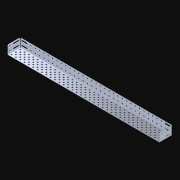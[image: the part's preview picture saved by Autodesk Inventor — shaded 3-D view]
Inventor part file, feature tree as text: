
AUTODESK INVENTOR PART (.ipt)
format: ipt  version: 2021 (Build 250183000, 183)  size: 3,463,680 bytes
history: native  units: in
note: dims shown in document units (in); Inventor stores cm internally (conversion verified against a paired STEP export)
features: other x240, extrude x239, pattern_linear x5, imported_body x1, sketch x1
ambient origin geometry x8: Origin, YZ Plane, XZ Plane, XY Plane, X Axis, Y Axis, Z Axis, Center Point
bodies: Body1 (feature_tree), Body2 (feature_tree), Body3 (feature_tree), Body4 (feature_tree), Body5 (feature_tree), Body6 (feature_tree), Body7 (feature_tree), Body8 (feature_tree), Body9 (feature_tree), Body10 (feature_tree), Body11 (feature_tree), Body12 (feature_tree), Body13 (feature_tree), Body14 (feature_tree), Body15 (feature_tree), Body16 (feature_tree), Body17 (feature_tree), Body18 (feature_tree), Body19 (feature_tree), Body20 (feature_tree), Body21 (feature_tree), Body22 (feature_tree), Body23 (feature_tree), Body24 (feature_tree), Body25 (feature_tree), Body26 (feature_tree), Body27 (feature_tree), Body28 (feature_tree), Body29 (feature_tree), Body30 (feature_tree), Body31 (feature_tree), Body32 (feature_tree), Body33 (feature_tree), Body34 (feature_tree), Body35 (feature_tree), Body36 (feature_tree), Body37 (feature_tree), Body38 (feature_tree), Body39 (feature_tree), Body40 (feature_tree), Body41 (feature_tree), Body42 (feature_tree), Body43 (feature_tree), Body44 (feature_tree), Body45 (feature_tree), Body46 (feature_tree), Body47 (feature_tree), Body48 (feature_tree), Body49 (feature_tree), Body50 (feature_tree), Body51 (feature_tree), Body52 (feature_tree), Body53 (feature_tree), Body54 (feature_tree), Body55 (feature_tree), Body56 (feature_tree), Body57 (feature_tree), Body58 (feature_tree), Body59 (feature_tree), Body60 (feature_tree), Body61 (feature_tree), Body62 (feature_tree), Body63 (feature_tree), Body64 (feature_tree), Body65 (feature_tree), Body66 (feature_tree), Body67 (feature_tree), Body68 (feature_tree), Body69 (feature_tree), Body70 (feature_tree), Body71 (feature_tree), Body72 (feature_tree), Body73 (feature_tree), Body74 (feature_tree), Body75 (feature_tree), Body76 (feature_tree), Body77 (feature_tree), Body78 (feature_tree), Body79 (feature_tree), Body80 (feature_tree), Body81 (feature_tree), Body82 (feature_tree), Body83 (feature_tree), Body84 (feature_tree), Body85 (feature_tree), Body86 (feature_tree), Body87 (feature_tree), Body88 (feature_tree), Body89 (feature_tree), Body90 (feature_tree), Body91 (feature_tree), Body92 (feature_tree), Body93 (feature_tree), Body94 (feature_tree), Body95 (feature_tree), Body96 (feature_tree), Body97 (feature_tree), Body98 (feature_tree), Body99 (feature_tree), Body100 (feature_tree), Body101 (feature_tree), Body102 (feature_tree), Body103 (feature_tree), Body104 (feature_tree), Body105 (feature_tree), Body106 (feature_tree), Body107 (feature_tree), Body108 (feature_tree), Body109 (feature_tree), Body110 (feature_tree), Body111 (feature_tree), Body112 (feature_tree), Body113 (feature_tree), Body114 (feature_tree), Body115 (feature_tree), Body116 (feature_tree), Body117 (feature_tree), Body118 (feature_tree), Body119 (feature_tree), Body120 (feature_tree), Body121 (feature_tree), Body122 (feature_tree), Body123 (feature_tree), Body124 (feature_tree), Body125 (feature_tree), Body126 (feature_tree), Body127 (feature_tree), Body128 (feature_tree), Body129 (feature_tree), Body130 (feature_tree), Body131 (feature_tree), Body132 (feature_tree), Body133 (feature_tree), Body134 (feature_tree), Body135 (feature_tree), Body136 (feature_tree), Body137 (feature_tree), Body138 (feature_tree), Body139 (feature_tree), Body140 (feature_tree), Body141 (feature_tree), Body142 (feature_tree), Body143 (feature_tree), Body144 (feature_tree), Body145 (feature_tree), Body146 (feature_tree), Body147 (feature_tree), Body148 (feature_tree), Body149 (feature_tree), Body150 (feature_tree), Body151 (feature_tree), Body152 (feature_tree), Body153 (feature_tree), Body154 (feature_tree), Body155 (feature_tree), Body156 (feature_tree), Body157 (feature_tree), Body158 (feature_tree), Body159 (feature_tree), Body160 (feature_tree), Body161 (feature_tree), Body162 (feature_tree), Body163 (feature_tree), Body164 (feature_tree), Body165 (feature_tree), Body166 (feature_tree), Body167 (feature_tree), Body168 (feature_tree), Body169 (feature_tree), Body170 (feature_tree), Body171 (feature_tree), Body172 (feature_tree), Body173 (feature_tree), Body174 (feature_tree), Body175 (feature_tree), Body176 (feature_tree), Body177 (feature_tree), Body178 (feature_tree), Body179 (feature_tree), Body180 (feature_tree), Body181 (feature_tree), Body182 (feature_tree), Body183 (feature_tree), Body184 (feature_tree), Body185 (feature_tree), Body186 (feature_tree), Body187 (feature_tree), Body188 (feature_tree), Body189 (feature_tree), Body190 (feature_tree), Body191 (feature_tree), Body192 (feature_tree), Body193 (feature_tree), Body194 (feature_tree), Body195 (feature_tree), Body196 (feature_tree), Body197 (feature_tree), Body198 (feature_tree), Body199 (feature_tree), Body200 (feature_tree), Body201 (feature_tree), Body202 (feature_tree), Body203 (feature_tree), Body204 (feature_tree), Body205 (feature_tree), Body206 (feature_tree), Body207 (feature_tree), Body208 (feature_tree), Body209 (feature_tree), Body210 (feature_tree), Body211 (feature_tree), Body212 (feature_tree), Body213 (feature_tree), Body214 (feature_tree), Body215 (feature_tree), Body216 (feature_tree), Body217 (feature_tree), Body218 (feature_tree), Body219 (feature_tree), Body220 (feature_tree), Body221 (feature_tree), Body222 (feature_tree), Body223 (feature_tree), Body224 (feature_tree), Body225 (feature_tree), Body226 (feature_tree), Body227 (feature_tree), Body228 (feature_tree), Body229 (feature_tree), Body230 (feature_tree), Body231 (feature_tree), Body232 (feature_tree), Body233 (feature_tree), Body234 (feature_tree), Body235 (feature_tree), Body236 (feature_tree), Body237 (feature_tree), Body238 (feature_tree), Body239 (feature_tree), Body240 (feature_tree)
feature tree (486):
  parser-record x1  (decoder bookkeeping rows leaked as tree rows — omitted from the tree; the rows remain in map.json)
  imported_body  "Base1"
  pattern_linear  "Rectangular Pattern1"  Count1=35 Spacing1=0.5in
  pattern_linear  "Rectangular Pattern2"  Count1=3 Spacing1=0.5in
  pattern_linear  "Rectangular Pattern3"  Spacing1=0.167in  [1 undecoded]
  pattern_linear  "Rectangular Pattern4"  Spacing1=0.046in  [1 undecoded]
  pattern_linear  "Rectangular Pattern5"  Count1=34 Spacing1=0.5in
  other  "Srf1"
  other  "Srf2"
  other  "Srf3"
  other  "Srf4"
  other  "Srf5"
  other  "Srf6"
  other  "Srf7"
  other  "Srf8"
  other  "Srf9"
  other  "Srf10"
  other  "Srf11"
  other  "Srf12"
  other  "Srf13"
  other  "Srf14"
  other  "Srf15"
  other  "Srf16"
  other  "Srf17"
  other  "Srf18"
  other  "Srf19"
  other  "Srf20"
  other  "Srf21"
  other  "Srf22"
  other  "Srf23"
  other  "Srf24"
  other  "Srf25"
  other  "Srf26"
  other  "Srf27"
  other  "Srf28"
  other  "Srf29"
  other  "Srf30"
  other  "Srf31"
  other  "Srf32"
  other  "Srf33"
  other  "Srf34"
  other  "Srf35"
  other  "Srf36"
  other  "Srf37"
  other  "Srf38"
  other  "Srf39"
  other  "Srf40"
  other  "Srf41"
  other  "Srf42"
  other  "Srf43"
  other  "Srf44"
  other  "Srf45"
  other  "Srf46"
  other  "Srf47"
  other  "Srf48"
  other  "Srf49"
  other  "Srf50"
  other  "Srf51"
  other  "Srf52"
  other  "Srf53"
  other  "Srf54"
  other  "Srf55"
  other  "Srf56"
  other  "Srf57"
  other  "Srf58"
  other  "Srf59"
  other  "Srf60"
  other  "Srf61"
  other  "Srf62"
  other  "Srf63"
  other  "Srf64"
  other  "Srf65"
  other  "Srf66"
  other  "Srf67"
  other  "Srf68"
  other  "Srf69"
  other  "Srf70"
  other  "Srf71"
  other  "Srf72"
  other  "Srf73"
  other  "Srf74"
  other  "Srf75"
  other  "Srf76"
  other  "Srf77"
  other  "Srf78"
  other  "Srf79"
  other  "Srf80"
  other  "Srf81"
  other  "Srf82"
  other  "Srf83"
  other  "Srf84"
  other  "Srf85"
  other  "Srf86"
  other  "Srf87"
  other  "Srf88"
  other  "Srf89"
  other  "Srf90"
  other  "Srf91"
  other  "Srf92"
  other  "Srf93"
  other  "Srf94"
  other  "Srf95"
  other  "Srf96"
  other  "Srf97"
  other  "Srf98"
  other  "Srf99"
  other  "Srf100"
  other  "Srf101"
  other  "Srf102"
  other  "Srf103"
  other  "Srf104"
  other  "Srf105"
  sketch  "Sketch10"  dims[d125=0.046in d126=0.0in d127=13.7795in d129=0.5in d130=1.1811in d132=0.5in d133=0.167in d134=0.046in d135=0.0in d136=13.3858in d138=0.5in d139=0.7874in d141=0.5in d143=0.046in d144=0.0in d145=0.7874in d147=0.5in d149=0.046in d150=0.0in d151=12.2047in d153=0.5in d154=0.7874in d156=0.5in d158=0.046in d159=0.0in d160=0.7874in d162=0.5in d163=0.0in d164=0.0in d165=0.0in d166=0.0in d167=0.0in d168=0.0in d169=0.0in d170=0.0in d171=0.0in d172=0.0in d173=0.0in d174=0.0in d175=0.0in d176=0.0in d177=0.0in d178=0.0in d179=0.0in d180=0.0in d181=0.0in d182=0.0in d183=0.0in d184=0.0in d185=0.0in d186=0.0in d187=0.0in d188=0.0in d189=0.0in d190=0.0in d191=0.0in d192=0.0in d193=0.0in d194=0.0in d195=0.0in d196=0.0in d197=0.0in d198=0.0in d199=0.0in d200=0.0in d201=0.0in d202=0.0in d203=0.0in d204=0.0in d205=0.0in d206=0.0in d207=0.0in d208=0.0in d209=0.0in d210=0.0in d211=0.0in d212=0.0in d213=0.0in d214=0.0in d215=0.0in d216=0.0in d217=0.0in d218=0.0in d219=0.0in d220=0.0in d221=0.0in d222=0.0in d223=0.0in d224=0.0in d225=0.0in d226=0.0in d227=0.0in d228=0.0in d229=0.0in d230=0.0in d231=0.0in d232=0.0in d233=0.0in d234=0.0in d235=0.0in d236=0.0in d237=0.0in d238=0.0in d239=0.0in d240=0.0in d241=0.0in d242=0.0in d243=0.0in d244=0.0in d245=0.0in d246=0.0in d247=0.0in d248=0.0in d249=0.0in d250=0.0in d251=0.0in d252=0.0in d253=0.0in d254=0.0in d255=0.0in d256=0.0in d257=0.0in d258=0.0in d259=0.0in d260=0.0in d261=0.0in d262=0.0in d263=0.0in d264=0.0in d265=0.0in d266=0.0in d267=0.0in d268=0.0in d269=0.0in d270=0.0in d271=0.0in d272=0.0in d273=0.0in d274=0.0in d275=0.0in d276=0.0in d277=0.0in d278=0.0in d279=0.0in d280=0.0in d281=0.0in d282=0.0in d283=0.0in d284=0.0in d285=0.0in d286=0.0in d287=0.0in d288=0.0in d289=0.0in d290=0.0in d291=0.0in d292=0.0in d293=0.0in d294=0.0in d295=0.0in d296=0.0in d297=0.0in d298=0.0in d299=0.0in d300=0.0in d301=0.0in d302=0.0in d303=0.0in d304=0.0in d305=0.0in d306=0.0in d307=0.0in d308=0.0in d309=0.0in d310=0.0in d311=0.0in d312=0.0in d313=0.0in d314=0.0in d315=0.0in d316=0.0in d317=0.0in d318=0.0in d319=0.0in d320=0.0in d321=0.0in d322=0.0in d323=0.0in d324=0.0in d325=0.0in d326=0.0in d327=0.0in d328=0.0in d329=0.0in d330=0.0in d331=0.0in d332=0.0in d333=0.0in d334=0.0in d335=0.0in d336=0.0in d337=0.0in d338=0.0in d339=0.0in d340=0.0in d341=0.0in d342=0.0in d343=0.0in d344=0.0in d345=0.0in d346=0.0in d347=0.0in d348=0.0in d349=0.0in d350=0.0in d351=0.0in d352=0.0in d353=0.0in d354=0.0in d355=0.0in d356=0.0in d357=0.0in d358=0.0in d359=0.0in d360=0.0in d361=0.0in d362=0.0in d363=0.0in d364=0.0in d365=0.0in d366=0.0in d367=0.0in d368=0.0in d369=0.0in d370=0.0in d371=0.0in d372=0.0in d373=0.0in d374=0.0in d375=0.0in d376=0.0in d377=0.0in d378=0.0in d379=0.0in d380=0.0in d381=0.0in d382=0.0in d383=0.0in d384=0.0in d385=0.0in d386=0.0in d387=0.0in d388=0.0in d389=0.0in d390=0.0in d391=0.0in d392=0.0in d393=0.0in d394=0.0in d395=0.0in d396=0.0in d397=0.0in d398=0.0in d399=0.0in d400=0.0in d401=0.0in d402=0.0in d403=0.0in d404=0.0in d405=0.0in d406=0.0in d407=0.0in d408=0.0in d409=0.0in d410=0.0in d411=0.0in d412=0.0in d413=0.0in d414=0.0in d415=0.0in d416=0.0in d417=0.0in d418=0.0in d419=0.0in d420=0.0in d421=0.0in d422=0.0in d423=0.0in d424=0.0in d425=0.0in d426=0.0in d427=0.0in d428=0.0in d429=0.0in d430=0.0in d431=0.0in d432=0.0in d433=0.0in d434=0.0in d435=0.0in d436=0.0in d437=0.0in d438=0.0in d439=0.0in d440=0.0in d441=0.0in d442=0.0in d443=0.0in d444=0.0in d445=0.0in d446=0.0in d447=0.0in d448=0.0in d449=0.0in d450=0.0in d451=0.0in d452=0.0in d453=0.0in d454=0.0in d455=0.0in d456=0.0in d457=0.0in d458=0.0in d459=0.0in d460=0.0in d461=0.0in d462=0.0in d463=0.0in d464=0.0in d465=0.0in d466=0.0in d467=0.0in d468=0.0in d469=0.0in d470=0.0in d471=0.0in d472=0.0in d473=0.0in d474=0.0in d475=0.0in d476=0.0in d477=0.0in d478=0.0in d479=0.0in d480=0.0in d481=0.0in d482=0.0in d483=0.0in d484=0.0in d485=0.0in d486=0.0in d487=0.0in d488=0.0in d489=0.0in d490=0.0in d491=0.0in d492=0.0in d493=0.0in d494=0.0in d495=0.0in d496=0.0in d497=0.0in d498=0.0in d499=0.0in d500=0.0in d501=0.0in d502=0.0in d503=0.0in d504=0.0in d505=0.0in d506=0.0in d507=0.0in d508=0.0in d509=0.0in d510=0.0in d511=0.0in d512=0.0in d513=0.0in d514=0.0in d515=0.0in d516=0.0in d517=0.0in d518=0.0in d519=0.0in d520=0.0in d521=0.0in d522=0.0in d523=0.0in d524=0.0in d525=0.0in d526=0.0in d527=0.0in d528=0.0in d529=0.0in d530=0.0in d531=0.0in d532=0.0in d533=0.0in d534=0.0in d535=0.0in d536=0.0in d537=0.0in d538=0.0in d539=0.0in d540=0.0in d541=0.0in d542=0.0in d543=0.0in d544=0.0in d545=0.0in d546=0.0in d547=0.0in d548=0.0in d549=0.0in d550=0.0in d551=0.0in d552=0.0in d553=0.0in d554=0.0in d555=0.0in d556=0.0in d557=0.0in d558=0.0in d559=0.0in d560=0.0in d561=0.0in d562=0.0in d563=0.0in d564=0.0in d565=0.0in d566=0.0in d567=0.0in d568=0.0in d569=0.0in d570=0.0in d571=0.0in d572=0.0in d573=0.0in d574=0.0in d575=0.0in d576=0.0in d577=0.0in d578=0.0in d579=0.0in d580=0.0in d581=0.0in d582=0.0in d583=0.0in d584=0.0in d585=0.0in d586=0.0in d587=0.0in d588=0.0in d589=0.0in d590=0.0in d591=0.0in d592=0.0in d593=0.0in d594=0.0in d595=0.0in d596=0.0in d597=0.0in d598=0.0in d599=0.0in d600=0.0in d601=0.0in d602=0.0in d603=0.0in d604=0.0in d605=0.0in d606=0.0in d607=0.0in d608=0.0in d609=0.0in d610=0.0in d611=0.0in d612=0.0in d613=0.0in d614=0.0in d615=0.0in d616=0.0in d617=0.0in d618=0.0in d619=0.0in d620=0.0in d621=0.0in d622=0.0in d623=0.0in d624=0.0in d625=0.0in d626=0.0in d627=0.0in d628=0.0in d629=0.0in d630=0.0in d631=0.0in d632=0.0in d633=0.0in d634=0.0in d635=0.0in d636=0.0in d637=0.0in d638=0.0in d639=0.0in d640=0.0in]
  other  "Srf106"
  other  "Srf107"
  other  "Srf108"
  other  "Srf109"
  other  "Srf110"
  other  "Srf111"
  other  "Srf112"
  other  "Srf113"
  other  "Srf114"
  other  "Srf115"
  other  "Srf116"
  other  "Srf117"
  other  "Srf118"
  other  "Srf119"
  other  "Srf120"
  other  "Srf121"
  other  "Srf122"
  other  "Srf123"
  other  "Srf124"
  other  "Srf125"
  other  "Srf126"
  other  "Srf127"
  other  "Srf128"
  other  "Srf129"
  other  "Srf130"
  other  "Srf131"
  other  "Srf132"
  other  "Srf133"
  other  "Srf134"
  other  "Srf135"
  other  "Srf136"
  other  "Srf137"
  other  "Srf138"
  other  "Srf139"
  other  "Srf140"
  other  "Srf141"
  other  "Srf142"
  other  "Srf143"
  other  "Srf144"
  other  "Srf145"
  other  "Srf146"
  other  "Srf147"
  other  "Srf148"
  other  "Srf149"
  other  "Srf150"
  other  "Srf151"
  other  "Srf152"
  other  "Srf153"
  other  "Srf154"
  other  "Srf155"
  other  "Srf156"
  other  "Srf157"
  other  "Srf158"
  other  "Srf159"
  other  "Srf160"
  other  "Srf161"
  other  "Srf162"
  other  "Srf163"
  other  "Srf164"
  other  "Srf165"
  other  "Srf166"
  other  "Srf167"
  other  "Srf168"
  other  "Srf169"
  other  "Srf170"
  other  "Srf171"
  other  "Srf172"
  other  "Srf173"
  other  "Srf174"
  other  "Srf175"
  other  "Srf176"
  other  "Srf177"
  other  "Srf178"
  other  "Srf179"
  other  "Srf180"
  other  "Srf181"
  other  "Srf182"
  other  "Srf183"
  other  "Srf184"
  other  "Srf185"
  other  "Srf186"
  other  "Srf187"
  other  "Srf188"
  other  "Srf189"
  other  "Srf190"
  other  "Srf191"
  other  "Srf192"
  other  "Srf193"
  other  "Srf194"
  other  "Srf195"
  other  "Srf196"
  other  "Srf197"
  other  "Srf198"
  other  "Srf199"
  other  "Srf200"
  other  "Srf201"
  other  "Srf202"
  other  "Srf203"
  other  "Srf204"
  other  "Srf205"
  other  "Srf206"
  other  "Srf207"
  other  "Srf208"
  other  "Srf209"
  other  "Srf210"
  other  "Srf211"
  other  "Srf212"
  other  "Srf213"
  other  "Srf214"
  other  "Srf215"
  other  "Srf216"
  other  "Srf217"
  other  "Srf218"
  other  "Srf219"
  other  "Srf220"
  other  "Srf221"
  other  "Srf222"
  other  "Srf223"
  other  "Srf224"
  other  "Srf225"
  other  "Srf226"
  other  "Srf227"
  other  "Srf228"
  other  "Srf229"
  other  "Srf230"
  other  "Srf231"
  other  "Srf232"
  other  "Srf233"
  other  "Srf234"
  other  "Srf235"
  other  "Srf236"
  other  "Srf237"
  other  "Srf238"
  other  "Srf239"
  extrude  "ExtrusionSrf1"  Depth=0.5in
  extrude  "ExtrusionSrf106"  Depth=0.046in TaperAngle=0.0deg
  extrude  "ExtrusionSrf174"  Depth=0.5in
  extrude  "ExtrusionSrf176"  Depth=0.046in TaperAngle=0.0deg
  extrude  "ExtrusionSrf238"  Depth=0.5in
  extrude  "ExtrusionSrf2"  Depth=0.5in
  extrude  "ExtrusionSrf3"  Depth=0.046in TaperAngle=0.0deg
  extrude  "ExtrusionSrf4"  Depth=0.5in
  extrude  "ExtrusionSrf5"  [1 undecoded]
  extrude  "ExtrusionSrf6"  [1 undecoded]
  extrude  "ExtrusionSrf7"  [1 undecoded]
  extrude  "ExtrusionSrf8"  [1 undecoded]
  extrude  "ExtrusionSrf9"  [1 undecoded]
  extrude  "ExtrusionSrf10"  [1 undecoded]
  extrude  "ExtrusionSrf11"  [1 undecoded]
  extrude  "ExtrusionSrf12"  [1 undecoded]
  extrude  "ExtrusionSrf13"  [1 undecoded]
  extrude  "ExtrusionSrf14"  [1 undecoded]
  extrude  "ExtrusionSrf15"  [1 undecoded]
  extrude  "ExtrusionSrf16"  [1 undecoded]
  extrude  "ExtrusionSrf17"  [1 undecoded]
  extrude  "ExtrusionSrf18"  [1 undecoded]
  extrude  "ExtrusionSrf19"  [1 undecoded]
  extrude  "ExtrusionSrf20"  [1 undecoded]
  extrude  "ExtrusionSrf21"  [1 undecoded]
  extrude  "ExtrusionSrf22"  [1 undecoded]
  extrude  "ExtrusionSrf23"  [1 undecoded]
  extrude  "ExtrusionSrf24"  [1 undecoded]
  extrude  "ExtrusionSrf25"  [1 undecoded]
  extrude  "ExtrusionSrf26"  [1 undecoded]
  extrude  "ExtrusionSrf27"  [1 undecoded]
  extrude  "ExtrusionSrf28"  [1 undecoded]
  extrude  "ExtrusionSrf29"  [1 undecoded]
  extrude  "ExtrusionSrf30"  [1 undecoded]
  extrude  "ExtrusionSrf31"  [1 undecoded]
  extrude  "ExtrusionSrf32"  [1 undecoded]
  extrude  "ExtrusionSrf33"  [1 undecoded]
  extrude  "ExtrusionSrf34"  [1 undecoded]
  extrude  "ExtrusionSrf35"  [1 undecoded]
  extrude  "ExtrusionSrf36"  [1 undecoded]
  extrude  "ExtrusionSrf37"  [1 undecoded]
  extrude  "ExtrusionSrf38"  [1 undecoded]
  extrude  "ExtrusionSrf39"  [1 undecoded]
  extrude  "ExtrusionSrf40"  [1 undecoded]
  extrude  "ExtrusionSrf41"  [1 undecoded]
  extrude  "ExtrusionSrf42"  [1 undecoded]
  extrude  "ExtrusionSrf43"  [1 undecoded]
  extrude  "ExtrusionSrf44"  [1 undecoded]
  extrude  "ExtrusionSrf45"  [1 undecoded]
  extrude  "ExtrusionSrf46"  [1 undecoded]
  extrude  "ExtrusionSrf47"  [1 undecoded]
  extrude  "ExtrusionSrf48"  [1 undecoded]
  extrude  "ExtrusionSrf49"  [1 undecoded]
  extrude  "ExtrusionSrf50"  [1 undecoded]
  extrude  "ExtrusionSrf51"  [1 undecoded]
  extrude  "ExtrusionSrf52"  [1 undecoded]
  extrude  "ExtrusionSrf53"  [1 undecoded]
  extrude  "ExtrusionSrf54"  [1 undecoded]
  extrude  "ExtrusionSrf55"  [1 undecoded]
  extrude  "ExtrusionSrf56"  [1 undecoded]
  extrude  "ExtrusionSrf57"  [1 undecoded]
  extrude  "ExtrusionSrf58"  [1 undecoded]
  extrude  "ExtrusionSrf59"  [1 undecoded]
  extrude  "ExtrusionSrf60"  [1 undecoded]
  extrude  "ExtrusionSrf61"  [1 undecoded]
  extrude  "ExtrusionSrf62"  [1 undecoded]
  extrude  "ExtrusionSrf63"  [1 undecoded]
  extrude  "ExtrusionSrf64"  [1 undecoded]
  extrude  "ExtrusionSrf65"  [1 undecoded]
  extrude  "ExtrusionSrf66"  [1 undecoded]
  extrude  "ExtrusionSrf67"  [1 undecoded]
  extrude  "ExtrusionSrf68"  [1 undecoded]
  extrude  "ExtrusionSrf69"  [1 undecoded]
  extrude  "ExtrusionSrf70"  [1 undecoded]
  extrude  "ExtrusionSrf71"  [1 undecoded]
  extrude  "ExtrusionSrf72"  [1 undecoded]
  extrude  "ExtrusionSrf73"  [1 undecoded]
  extrude  "ExtrusionSrf74"  [1 undecoded]
  extrude  "ExtrusionSrf75"  [1 undecoded]
  extrude  "ExtrusionSrf76"  [1 undecoded]
  extrude  "ExtrusionSrf77"  [1 undecoded]
  extrude  "ExtrusionSrf78"  [1 undecoded]
  extrude  "ExtrusionSrf79"  [1 undecoded]
  extrude  "ExtrusionSrf80"  [1 undecoded]
  extrude  "ExtrusionSrf81"  [1 undecoded]
  extrude  "ExtrusionSrf82"  [1 undecoded]
  extrude  "ExtrusionSrf83"  [1 undecoded]
  extrude  "ExtrusionSrf84"  [1 undecoded]
  extrude  "ExtrusionSrf85"  [1 undecoded]
  extrude  "ExtrusionSrf86"  [1 undecoded]
  extrude  "ExtrusionSrf87"  [1 undecoded]
  extrude  "ExtrusionSrf88"  [1 undecoded]
  extrude  "ExtrusionSrf89"  [1 undecoded]
  extrude  "ExtrusionSrf90"  [1 undecoded]
  extrude  "ExtrusionSrf91"  [1 undecoded]
  extrude  "ExtrusionSrf92"  [1 undecoded]
  extrude  "ExtrusionSrf93"  [1 undecoded]
  extrude  "ExtrusionSrf94"  [1 undecoded]
  extrude  "ExtrusionSrf95"  [1 undecoded]
  extrude  "ExtrusionSrf96"  [1 undecoded]
  extrude  "ExtrusionSrf97"  [1 undecoded]
  extrude  "ExtrusionSrf98"  [1 undecoded]
  extrude  "ExtrusionSrf99"  [1 undecoded]
  extrude  "ExtrusionSrf100"  [1 undecoded]
  extrude  "ExtrusionSrf101"  [1 undecoded]
  extrude  "ExtrusionSrf102"  [1 undecoded]
  extrude  "ExtrusionSrf103"  [1 undecoded]
  extrude  "ExtrusionSrf104"  [1 undecoded]
  extrude  "ExtrusionSrf105"  [1 undecoded]
  extrude  "ExtrusionSrf107"  [1 undecoded]
  extrude  "ExtrusionSrf108"  [1 undecoded]
  extrude  "ExtrusionSrf109"  [1 undecoded]
  extrude  "ExtrusionSrf110"  [1 undecoded]
  extrude  "ExtrusionSrf111"  [1 undecoded]
  extrude  "ExtrusionSrf112"  [1 undecoded]
  extrude  "ExtrusionSrf113"  [1 undecoded]
  extrude  "ExtrusionSrf114"  [1 undecoded]
  extrude  "ExtrusionSrf115"  [1 undecoded]
  extrude  "ExtrusionSrf116"  [1 undecoded]
  extrude  "ExtrusionSrf117"  [1 undecoded]
  extrude  "ExtrusionSrf118"  [1 undecoded]
  extrude  "ExtrusionSrf119"  [1 undecoded]
  extrude  "ExtrusionSrf120"  [1 undecoded]
  extrude  "ExtrusionSrf121"  [1 undecoded]
  extrude  "ExtrusionSrf122"  [1 undecoded]
  extrude  "ExtrusionSrf123"  [1 undecoded]
  extrude  "ExtrusionSrf124"  [1 undecoded]
  extrude  "ExtrusionSrf125"  [1 undecoded]
  extrude  "ExtrusionSrf126"  [1 undecoded]
  extrude  "ExtrusionSrf127"  [1 undecoded]
  extrude  "ExtrusionSrf128"  [1 undecoded]
  extrude  "ExtrusionSrf129"  [1 undecoded]
  extrude  "ExtrusionSrf130"  [1 undecoded]
  extrude  "ExtrusionSrf131"  [1 undecoded]
  extrude  "ExtrusionSrf132"  [1 undecoded]
  extrude  "ExtrusionSrf133"  [1 undecoded]
  extrude  "ExtrusionSrf134"  [1 undecoded]
  extrude  "ExtrusionSrf135"  [1 undecoded]
  extrude  "ExtrusionSrf136"  [1 undecoded]
  extrude  "ExtrusionSrf137"  [1 undecoded]
  extrude  "ExtrusionSrf138"  [1 undecoded]
  extrude  "ExtrusionSrf139"  [1 undecoded]
  extrude  "ExtrusionSrf140"  [1 undecoded]
  extrude  "ExtrusionSrf141"  [1 undecoded]
  extrude  "ExtrusionSrf142"  [1 undecoded]
  extrude  "ExtrusionSrf143"  [1 undecoded]
  extrude  "ExtrusionSrf144"  [1 undecoded]
  extrude  "ExtrusionSrf145"  [1 undecoded]
  extrude  "ExtrusionSrf146"  [1 undecoded]
  extrude  "ExtrusionSrf147"  [1 undecoded]
  extrude  "ExtrusionSrf148"  [1 undecoded]
  extrude  "ExtrusionSrf149"  [1 undecoded]
  extrude  "ExtrusionSrf150"  [1 undecoded]
  extrude  "ExtrusionSrf151"  [1 undecoded]
  extrude  "ExtrusionSrf152"  [1 undecoded]
  extrude  "ExtrusionSrf153"  [1 undecoded]
  extrude  "ExtrusionSrf154"  [1 undecoded]
  extrude  "ExtrusionSrf155"  [1 undecoded]
  extrude  "ExtrusionSrf156"  [1 undecoded]
  extrude  "ExtrusionSrf157"  [1 undecoded]
  extrude  "ExtrusionSrf158"  [1 undecoded]
  extrude  "ExtrusionSrf159"  [1 undecoded]
  extrude  "ExtrusionSrf160"  [1 undecoded]
  extrude  "ExtrusionSrf161"  [1 undecoded]
  extrude  "ExtrusionSrf162"  [1 undecoded]
  extrude  "ExtrusionSrf163"  [1 undecoded]
  extrude  "ExtrusionSrf164"  [1 undecoded]
  extrude  "ExtrusionSrf165"  [1 undecoded]
  extrude  "ExtrusionSrf166"  [1 undecoded]
  extrude  "ExtrusionSrf167"  [1 undecoded]
  extrude  "ExtrusionSrf168"  [1 undecoded]
  extrude  "ExtrusionSrf169"  [1 undecoded]
  extrude  "ExtrusionSrf170"  [1 undecoded]
  extrude  "ExtrusionSrf171"  [1 undecoded]
  extrude  "ExtrusionSrf172"  [1 undecoded]
  extrude  "ExtrusionSrf173"  [1 undecoded]
  extrude  "ExtrusionSrf175"  [1 undecoded]
  extrude  "ExtrusionSrf177"  [1 undecoded]
  extrude  "ExtrusionSrf178"  [1 undecoded]
  extrude  "ExtrusionSrf179"  [1 undecoded]
  extrude  "ExtrusionSrf180"  [1 undecoded]
  extrude  "ExtrusionSrf181"  [1 undecoded]
  extrude  "ExtrusionSrf182"  [1 undecoded]
  extrude  "ExtrusionSrf183"  [1 undecoded]
  extrude  "ExtrusionSrf184"  [1 undecoded]
  extrude  "ExtrusionSrf185"  [1 undecoded]
  extrude  "ExtrusionSrf186"  [1 undecoded]
  extrude  "ExtrusionSrf187"  [1 undecoded]
  extrude  "ExtrusionSrf188"  [1 undecoded]
  extrude  "ExtrusionSrf189"  [1 undecoded]
  extrude  "ExtrusionSrf190"  [1 undecoded]
  extrude  "ExtrusionSrf191"  [1 undecoded]
  extrude  "ExtrusionSrf192"  [1 undecoded]
  extrude  "ExtrusionSrf193"  [1 undecoded]
  extrude  "ExtrusionSrf194"  [1 undecoded]
  extrude  "ExtrusionSrf195"  [1 undecoded]
  extrude  "ExtrusionSrf196"  [1 undecoded]
  extrude  "ExtrusionSrf197"  [1 undecoded]
  extrude  "ExtrusionSrf198"  [1 undecoded]
  extrude  "ExtrusionSrf199"  [1 undecoded]
  extrude  "ExtrusionSrf200"  [1 undecoded]
  extrude  "ExtrusionSrf201"  [1 undecoded]
  extrude  "ExtrusionSrf202"  [1 undecoded]
  extrude  "ExtrusionSrf203"  [1 undecoded]
  extrude  "ExtrusionSrf204"  [1 undecoded]
  extrude  "ExtrusionSrf205"  [1 undecoded]
  extrude  "ExtrusionSrf206"  [1 undecoded]
  extrude  "ExtrusionSrf207"  [1 undecoded]
  extrude  "ExtrusionSrf208"  [1 undecoded]
  extrude  "ExtrusionSrf209"  [1 undecoded]
  extrude  "ExtrusionSrf210"  [1 undecoded]
  extrude  "ExtrusionSrf211"  [1 undecoded]
  extrude  "ExtrusionSrf212"  [1 undecoded]
  extrude  "ExtrusionSrf213"  [1 undecoded]
  extrude  "ExtrusionSrf214"  [1 undecoded]
  extrude  "ExtrusionSrf215"  [1 undecoded]
  extrude  "ExtrusionSrf216"  [1 undecoded]
  extrude  "ExtrusionSrf217"  [1 undecoded]
  extrude  "ExtrusionSrf218"  [1 undecoded]
  extrude  "ExtrusionSrf219"  [1 undecoded]
  extrude  "ExtrusionSrf220"  [1 undecoded]
  extrude  "ExtrusionSrf221"  [1 undecoded]
  extrude  "ExtrusionSrf222"  [1 undecoded]
  extrude  "ExtrusionSrf223"  [1 undecoded]
  extrude  "ExtrusionSrf224"  [1 undecoded]
  extrude  "ExtrusionSrf225"  [1 undecoded]
  extrude  "ExtrusionSrf226"  [1 undecoded]
  extrude  "ExtrusionSrf227"  [1 undecoded]
  extrude  "ExtrusionSrf228"  [1 undecoded]
  extrude  "ExtrusionSrf229"  [1 undecoded]
  extrude  "ExtrusionSrf230"  [1 undecoded]
  extrude  "ExtrusionSrf231"  [1 undecoded]
  extrude  "ExtrusionSrf232"  [1 undecoded]
  extrude  "ExtrusionSrf233"  [1 undecoded]
  extrude  "ExtrusionSrf234"  [1 undecoded]
  extrude  "ExtrusionSrf235"  [1 undecoded]
  extrude  "ExtrusionSrf236"  [1 undecoded]
  extrude  "ExtrusionSrf237"  [1 undecoded]
  extrude  "ExtrusionSrf239"  [1 undecoded]
note: 233 required parameter values undecoded (feature->parameter linkage not recoverable at this tier; creation-order binding heuristic only, values carry confidence <= 0.55)
